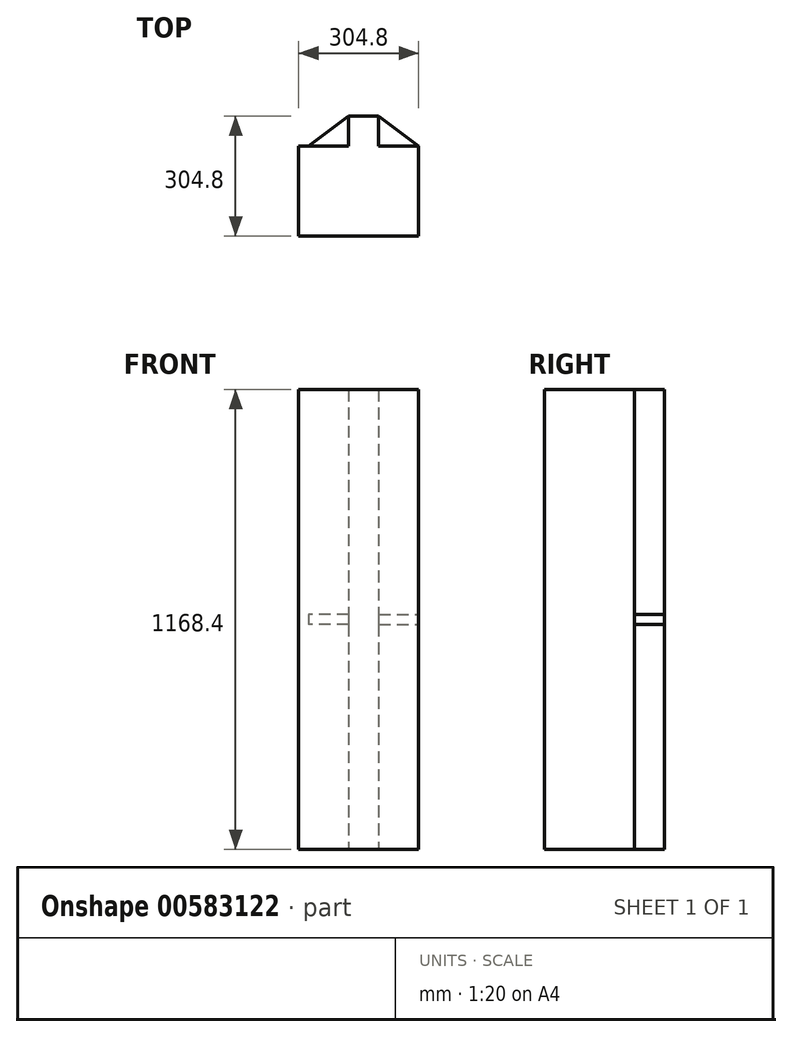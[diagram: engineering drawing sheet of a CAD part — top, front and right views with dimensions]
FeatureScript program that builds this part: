
annotation { "Feature Type Name" : "Feature", "Feature Type Description" : "" }
export const myFeature = defineFeature(function(context is Context, id is Id, definition is map)
    precondition{}
    {
        {
            var Q0;
            Q0=qCreatedBy(makeId("Top.planeOp"),FACE);
            var sketch = newSketch(context, id + "F0", { "sketchPlane" : qUnion([Q0])});
            skLineSegment(sketch, "E0", {"start": v(0, 0) * mm, "end": v(-76.2, 0) * mm});
            skLineSegment(sketch, "E1", {"start": v(-76.2, 0) * mm, "end": v(-76.2, 76.2) * mm});
            skLineSegment(sketch, "E2", {"start": v(0, 0) * mm, "end": v(0, 76.2) * mm});
            skLineSegment(sketch, "E3", {"start": v(0, 76.2) * mm, "end": v(-76.2, 76.2) * mm});
            skLineSegment(sketch, "E4", {"start": v(0, 76.2) * mm, "end": v(101.6, 0) * mm});
            skLineSegment(sketch, "E5", {"start": v(0, 0) * mm, "end": v(101.6, 0) * mm});
            skLineSegment(sketch, "E6.bottom", {"start": v(-76.2, 0) * mm, "end": v(101.6, 0) * mm});
            skLineSegment(sketch, "E6.top", {"start": v(-76.2, -228.6) * mm, "end": v(101.6, -228.6) * mm});
            skLineSegment(sketch, "E6.left", {"start": v(-76.2, 0) * mm, "end": v(-76.2, -228.6) * mm});
            skLineSegment(sketch, "E6.right", {"start": v(101.6, 0) * mm, "end": v(101.6, -228.6) * mm});
            skLineSegment(sketch, "E7", {"start": v(-177.8, 0) * mm, "end": v(-50.8, 0) * mm});
            skLineSegment(sketch, "E8", {"start": v(-76.2, 76.2) * mm, "end": v(-177.8, 0) * mm});
            skLineSegment(sketch, "E9.bottom", {"start": v(-76.2, -228.6) * mm, "end": v(-203.2, -228.6) * mm});
            skLineSegment(sketch, "E9.top", {"start": v(-76.2, 0) * mm, "end": v(-203.2, 0) * mm});
            skLineSegment(sketch, "E9.left", {"start": v(-76.2, -228.6) * mm, "end": v(-76.2, 0) * mm});
            skLineSegment(sketch, "E9.right", {"start": v(-203.2, -228.6) * mm, "end": v(-203.2, 0) * mm});
            skSolve(sketch);
        }
        {
            var Q0;
            Q0=makeQuery(id+"F0.imprint","IMPRINT",FACE,{"disambiguationData":[TD([[makeQuery(id+"F0.imprint","IMPRINT",EDGE,{"derivedFrom":sQuery(id+"F0.wireOp",EDGE,"E1")}),-1.0]])]});
            extrude(context, id + "F1", {"entities" : qUnion([Q0]), "endBound" : BoundingType.SYMMETRIC, "depth" : 1143 * mm, "offsetDistance" : 25.4 * mm});
        }
        {
            var Q0;
            {var subQ0=sQuery(id+"F0.wireOp",EDGE,"E1");Q0=makeQuery(id+"F0.imprint","IMPRINT",FACE,{"disambiguationData":[TD([[makeQuery(id+"F0.imprint","IMPRINT",EDGE,{"derivedFrom":subQ0}),1.0]])]});}
            var Q1;
            {var subQ0=sQuery(id+"F0.wireOp",EDGE,"E2");Q1=makeQuery(id+"F0.imprint","IMPRINT",FACE,{"disambiguationData":[TD([[makeQuery(id+"F0.imprint","IMPRINT",EDGE,{"derivedFrom":subQ0}),-1.0]])]});}
            extrude(context, id + "F2", {"entities" : qUnion([Q0, Q1]), "operationType" : NewBodyOperationType.ADD, "depth" : 25.4 * mm, "offsetDistance" : 25.4 * mm});
        }
        {
            var Q0;
            Q0=makeQuery(id+"F0.imprint","IMPRINT",FACE,{"disambiguationData":[TD([[makeQuery(id+"F0.imprint","IMPRINT",EDGE,{"derivedFrom":sQuery(id+"F0.wireOp",EDGE,"E9.bottom")}),-1.0]])]});
            var Q1;
            Q1=makeQuery(id+"F0.imprint","IMPRINT",FACE,{"disambiguationData":[TD([[makeQuery(id+"F0.imprint","IMPRINT",EDGE,{"derivedFrom":sQuery(id+"F0.wireOp",EDGE,"E6.top")}),1.0]])]});
            extrude(context, id + "F3", {"entities" : qUnion([Q0, Q1]), "operationType" : NewBodyOperationType.ADD, "endBound" : BoundingType.SYMMETRIC, "depth" : 1143 * mm, "offsetDistance" : 25.4 * mm});
        }
        {
            var Q0;
            {var subQ0=sQuery(id+"F0.wireOp",EDGE,"E7");var subQ1=sQuery(id+"F0.wireOp",EDGE,"E6.bottom");Q0=makeQuery(id+"F3.boolean.opBoolean","MERGE",FACE,{"derivedFrom":[makeQuery(id+"F1.opExtrude","CAP_FACE",FACE,{"disambiguationData":[OSD([sQuery(id+"F0.wireOp",EDGE,"E1"),sQuery(id+"F0.wireOp",EDGE,"E2"),sQuery(id+"F0.wireOp",EDGE,"E3"),subQ1,subQ0])],"isStart":false}),makeQuery(id+"F3.opExtrude","CAP_FACE",FACE,{"disambiguationData":[OSD([subQ1,sQuery(id+"F0.wireOp",EDGE,"E6.top"),sQuery(id+"F0.wireOp",EDGE,"E6.right"),subQ0,sQuery(id+"F0.wireOp",EDGE,"E9.bottom"),sQuery(id+"F0.wireOp",EDGE,"E9.top"),sQuery(id+"F0.wireOp",EDGE,"E9.right")])],"isStart":false})]});}
            extrude(context, id + "F4", {"entities" : qUnion([Q0]), "operationType" : NewBodyOperationType.ADD, "depth" : 25.4 * mm, "offsetDistance" : 25.4 * mm});
        }
    });
